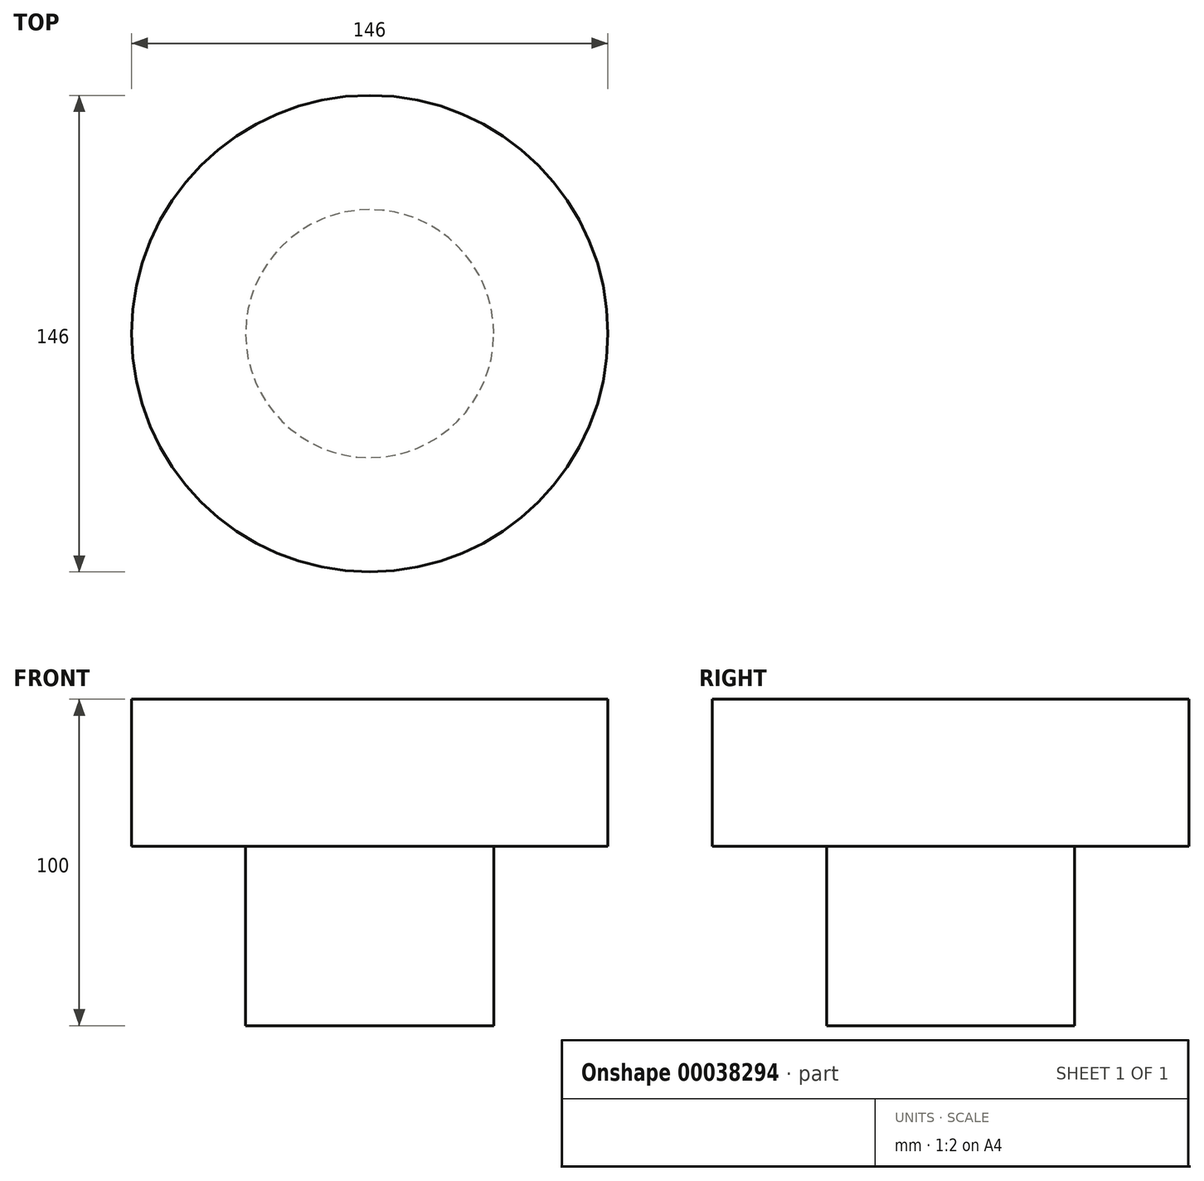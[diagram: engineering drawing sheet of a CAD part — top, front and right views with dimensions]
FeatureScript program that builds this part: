
annotation { "Feature Type Name" : "Feature", "Feature Type Description" : "" }
export const myFeature = defineFeature(function(context is Context, id is Id, definition is map)
    precondition{}
    {
        {
            var Q0;
            Q0=qCreatedBy(makeId("Front.planeOp"),FACE);
            var sketch = newSketch(context, id + "F0", { "sketchPlane" : qUnion([Q0])});
            skLineSegment(sketch, "E0", {"start": v(-121.55, 37) * mm, "end": v(-48.55, 37) * mm});
            skLineSegment(sketch, "E1", {"start": v(-48.55, 37) * mm, "end": v(-48.55, -63) * mm});
            skLineSegment(sketch, "E2", {"start": v(-48.55, -63) * mm, "end": v(-86.55, -63) * mm});
            skLineSegment(sketch, "E3", {"start": v(-86.55, -63) * mm, "end": v(-86.55, -8) * mm});
            skLineSegment(sketch, "E4", {"start": v(-86.55, -8) * mm, "end": v(-121.55, -8) * mm});
            skLineSegment(sketch, "E5", {"start": v(-121.55, 37) * mm, "end": v(-121.55, -8) * mm});
            skSolve(sketch);
        }
        {
            var Q0;
            Q0=makeQuery(id+"F0.imprint","IMPRINT",FACE,{"disambiguationData":[TD([[makeQuery(id+"F0.imprint","IMPRINT",EDGE,{"derivedFrom":sQuery(id+"F0.wireOp",EDGE,"E0")}),-1.0]])]});
            var Q1;
            Q1=sQuery(id+"F0.wireOp",EDGE,"E1");
            revolve(context, id + "F1", {"entities" : qUnion([Q0]), "axis" : qUnion([Q1]), "revolveType" : RevolveType.FULL});
        }
    });
